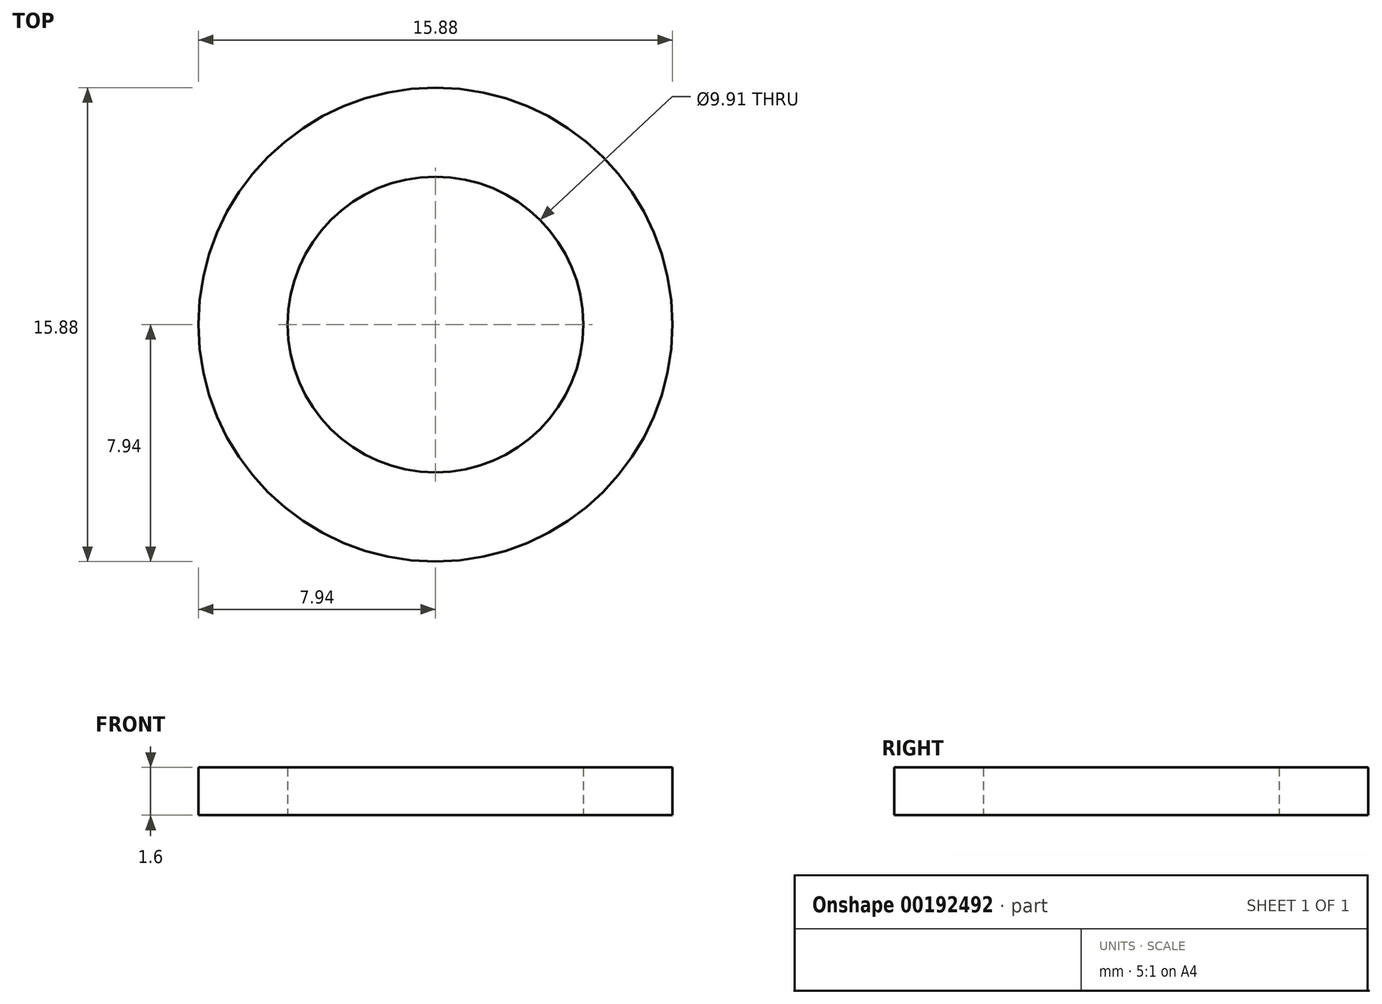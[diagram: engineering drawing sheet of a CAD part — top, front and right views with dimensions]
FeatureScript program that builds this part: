
annotation { "Feature Type Name" : "Feature", "Feature Type Description" : "" }
export const myFeature = defineFeature(function(context is Context, id is Id, definition is map)
    precondition{}
    {
        {
            var Q0;
            Q0=qCreatedBy(makeId("Top.planeOp"),FACE);
            var sketch = newSketch(context, id + "F0", { "sketchPlane" : qUnion([Q0])});
            skCircle(sketch, "E0", {"center": v(0, 0) * mm, "radius": 7.94 * mm});
            skCircle(sketch, "E1", {"center": v(0, 0) * mm, "radius": 4.95 * mm});
            skSolve(sketch);
        }
        {
            var Q0;
            Q0 = qSketchRegion(id + "F0", true);
            extrude(context, id + "F1", {"entities" : qUnion([Q0]), "depth" : 1.6 * mm});
        }
    });
